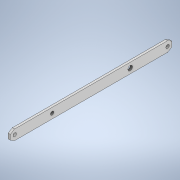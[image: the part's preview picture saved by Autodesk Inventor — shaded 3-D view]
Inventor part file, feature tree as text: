
AUTODESK INVENTOR PART (.ipt)
format: ipt  version: 2020 (Build 240168000, 168)  size: 216,576 bytes
history: native  units: in
note: dims shown in document units (in); Inventor stores cm internally (conversion verified against a paired STEP export)
features: extrude x5, sketch x5, other x3, projected_geometry x3
ambient origin geometry x8: Origin, YZ Plane, XZ Plane, XY Plane, X Axis, Y Axis, Z Axis, Center Point
bodies: Solid1 (feature_tree)
feature tree (16):
  other  "HexWheelGuard.ipt"
  extrude  "Extrusion1"  TaperAngle=0.0deg  [1 undecoded]
  extrude  "Extrusion2"  Depth=0.3937in
  extrude  "Extrusion3"  Depth=0.3937in TaperAngle=0.0deg
  extrude  "Extrusion4"  Depth=0.3543in
  extrude  "Extrusion5"  [1 undecoded]
  other  "Solid1::HexWheelGuard.ipt"
  other  "TaggingFeature1"
  sketch  "Sketch1"  dims[d0=0.3937in d1=0.0in d2=0.0in]
  projected_geometry  "Projected Loop1"
  sketch  "Sketch2"  dims[d3=0.3937in d4=0.0in d5=0.122in]
  sketch  "Sketch3"  dims[d6=0.122in d7=0.3937in d8=0.0in]
  sketch  "Sketch4"  dims[d10=0.3937in d11=0.0in d12=0.3543in]
  projected_geometry  "Projected Loop2"
  sketch  "Sketch5"  dims[d13=0.0787in d14=0.0in]
  projected_geometry  "Projected Loop3"
note: 2 required parameter values undecoded (feature->parameter linkage not recoverable at this tier; creation-order binding heuristic only, values carry confidence <= 0.55)
